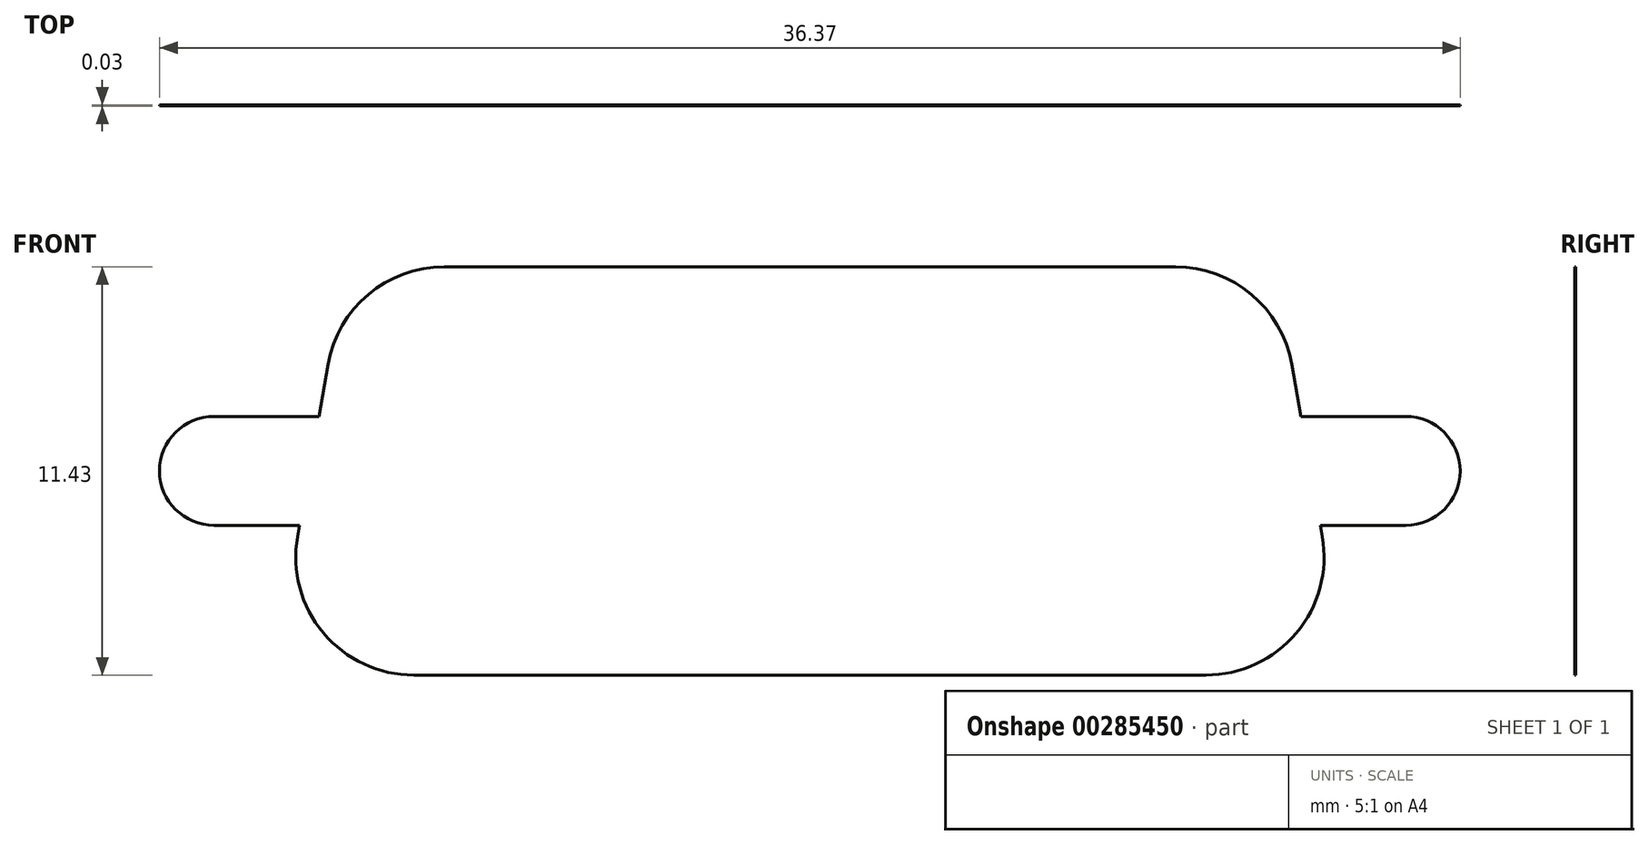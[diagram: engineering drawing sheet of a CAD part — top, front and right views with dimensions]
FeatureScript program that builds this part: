
annotation { "Feature Type Name" : "Feature", "Feature Type Description" : "" }
export const myFeature = defineFeature(function(context is Context, id is Id, definition is map)
    precondition{}
    {
        {
            var Q0;
            Q0=qCreatedBy(makeId("Front.planeOp"),FACE);
            var sketch = newSketch(context, id + "F0", { "sketchPlane" : qUnion([Q0])});
            skLineSegment(sketch, "E0.bottom", {"start": v(0, 0) * mm, "end": v(33.32, 0) * mm, "construction": true});
            skLineSegment(sketch, "E0.top", {"start": v(0, 11.43) * mm, "end": v(33.32, 11.43) * mm, "construction": true});
            skLineSegment(sketch, "E0.left", {"start": v(0, 0) * mm, "end": v(0, 11.43) * mm, "construction": true});
            skLineSegment(sketch, "E0.right", {"start": v(33.32, 0) * mm, "end": v(33.32, 11.43) * mm, "construction": true});
            skLineSegment(sketch, "E1", {"start": v(3.19, 8.7) * mm, "end": v(2.93, 7.24) * mm});
            skLineSegment(sketch, "E2", {"start": v(30.14, 8.7) * mm, "end": v(30.4, 7.24) * mm});
            skLineSegment(sketch, "E3", {"start": v(16.66, 11.43) * mm, "end": v(16.66, 0) * mm, "construction": true});
            skArc(sketch, "E4", {"start": v(0, 7.24) * mm, "mid": v(-1.52, 5.72) * mm, "end": v(0, 4.2) * mm});
            skArc(sketch, "E5", {"start": v(33.32, 4.2) * mm, "mid": v(34.85, 5.72) * mm, "end": v(33.32, 7.24) * mm});
            skLineSegment(sketch, "E6", {"start": v(0, 5.72) * mm, "end": v(33.32, 5.72) * mm, "construction": true});
            skLineSegment(sketch, "E7", {"start": v(6.44, 11.43) * mm, "end": v(26.89, 11.43) * mm});
            skLineSegment(sketch, "E8", {"start": v(27.74, 0) * mm, "end": v(5.59, 0) * mm});
            skPoint(sketch, "E9.visualSharp", {"position": v(3.67, 11.43) * mm});
            skArc(sketch, "E9.filletArc", {"start": v(6.44, 11.43) * mm, "mid": v(4.32, 10.66) * mm, "end": v(3.19, 8.7) * mm});
            skPoint(sketch, "E10.visualSharp", {"position": v(29.66, 11.43) * mm});
            skArc(sketch, "E10.filletArc", {"start": v(30.14, 8.7) * mm, "mid": v(29, 10.66) * mm, "end": v(26.89, 11.43) * mm});
            skPoint(sketch, "E11.visualSharp", {"position": v(31.67, 0) * mm});
            skArc(sketch, "E11.filletArc", {"start": v(27.74, 0) * mm, "mid": v(30.27, 1.18) * mm, "end": v(30.99, 3.88) * mm});
            skPoint(sketch, "E12.visualSharp", {"position": v(1.65, 0) * mm});
            skArc(sketch, "E12.filletArc", {"start": v(2.34, 3.88) * mm, "mid": v(3.06, 1.18) * mm, "end": v(5.59, 0) * mm});
            skLineSegment(sketch, "E13", {"start": v(0, 7.24) * mm, "end": v(2.93, 7.24) * mm});
            skLineSegment(sketch, "E14", {"start": v(0, 4.2) * mm, "end": v(2.4, 4.2) * mm});
            skLineSegment(sketch, "E15", {"start": v(33.32, 7.24) * mm, "end": v(30.4, 7.24) * mm});
            skLineSegment(sketch, "E16", {"start": v(33.32, 4.2) * mm, "end": v(30.93, 4.2) * mm});
            skLineSegment(sketch, "E17.trimOffspring", {"start": v(30.93, 4.2) * mm, "end": v(30.99, 3.88) * mm});
            skLineSegment(sketch, "E18.trimOffspring", {"start": v(2.4, 4.2) * mm, "end": v(2.34, 3.88) * mm});
            skSolve(sketch);
        }
        {
            var Q0;
            Q0 = qSketchRegion(id + "F0", true);
            extrude(context, id + "F1", {"entities" : qUnion([Q0]), "depth" : 0.03 * mm});
        }
    });
